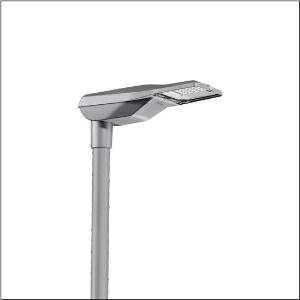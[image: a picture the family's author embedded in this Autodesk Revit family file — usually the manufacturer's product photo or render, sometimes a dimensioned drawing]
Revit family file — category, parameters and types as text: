
# Revit family: streetlight_sl_21_iq_micro___st1_0a_5xe1d61d08cb_4c5c
name_source: partatom
category: Lighting Fixtures
units: mm (PartAtom-declared; Revit-internal decimal feet)

## family parameters
Cut with Voids When Loaded = No
Host = Face
Light Source = No
Part Type = Normal
Room Calculation Point = No
Round Connector Dimension = Use Diameter
Shared = No

## types (1)
- --- (1 x LED, 2570 lm, 19.4 W, 2700K)
    Apparent Load = 19 VA
    CIE Flux Codes = 37 72 97 100 100
    Color Rendering = 70
    Color Temperature = 2700K
    Default Elevation = 1800 mm
    Description = Streetlight SL 21 iQ micro, mast luminaire, primary light control with lens, of PMMA, primary optical cover: cover, of toughened safety glass, transparent, light distribution: ST1.0a, light emission: direct distribution, primary light characteristic: asymmetric, installation type: post-top, side-entry, LED, High Power LED, rated luminous flux: 2.570lm, luminous efficacy: 133lm/W, light colour: 727, colour temperature: 2700K, control: Auto-Match, Temp-Guard, Lumen-Switch, Night-Set, Smart-Wire, Light-Fading, Desk-Remote (wireless, voltage-free reading and setting of iQ features in the workshop via application-optimized NFC function/RFID function), optimised constant luminous flux control (CLO 2.0), presetting dimming linear, mains connection: 220..240V, AC, 50/60Hz, start of lifetime: 19W, end of service life: 20W, reduction: 10W, luminaire housing, of diecast aluminium, powder-coated, Siteco® metallic grey (DB 702S), corrosivity category C5 mid according to DIN EN ISO 12944, please order mast flange separately, inclination adjustable: 0°, 5°, 10°, 15°, sealing non-destructively replaceable, multi-level sealing system, length: 528mm, width: 235mm, height: 110mm, mast flange for spigot size: 42mm (side-entry): 5XC10008XM4, 60/48mm (side-entry/post-top): 5XC10108XM2, 76/60mm (side-entry/post-top): 5XC10108XM1, protection rating (complete): IP66, insulation class (complete): insulation class II (safety insulation), certification: CE, ENEC, ENEC+, VDE, impact resistance: IK09, permissible operating ambient temperature for outdoor applications: -40..+50°C, standard-compliant lighting for roads and squares, packaging unit: 1 piece

Light Distribution: ST1.0a
    Height = 110 mm
    Lamp = 1 x LED
    Lamp Light Flux = 2570 lm
    Lamp Power = 19.4 W
    Lamp count = 1
    Length = 528 mm
    Luminous efficacy = 132 lm/W
    Manufacturer = Siteco
    ModVariant = No
    Model = 5XE1D61D08CB
    Number of Poles = 1
    OnlyDefault = Yes
    Power Factor = 1
    Product Name = Streetlight SL 21 iQ micro | ST1.0a
    Product group = mast luminaire | pylon top
    ProductGroupID = 6100
    Protection Class = Protection class II
    Protection Degree = IP 66
    RLX_Detail_Level = 1
    RLX_Emergency_Light_Flux = 0 lm
    RLX_Emergency_Type = 0
    RLX_Emergency_Type_DB = No
    RlxData = <blob elided: 99157 chars, md5=8cb5c1ab>
    Socket = socket
    Standby Power = 0 W
    System Light Flux = 2570 lm
    System Power = 19 W
    Type Comments = factory setting: luminous flux: 100 % | dim-lin: 254 | 387 mA
    Type Image = l_1006881.jpg
    URL = http://relux.com
    VarID = @adj_088513
    Voltage = 0 V
    Weight = 0.00 kg
    Width = 235 mm

## geometry (parser evidence)
native form markers: Blend x4, Sweep x11
no freeform markers — native parametric forms only
